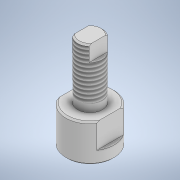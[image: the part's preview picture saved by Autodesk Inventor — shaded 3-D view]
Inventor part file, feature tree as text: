
AUTODESK INVENTOR PART (.ipt)
format: ipt  version: 2021 (Build 250183000, 183)  size: 157,184 bytes
history: native  units: mm
features: sketch x5, extrude x4, chamfer x2, thread x1, hole x1, projected_geometry x1
ambient origin geometry x8: Origin, YZ Plane, XZ Plane, XY Plane, X Axis, Y Axis, Z Axis, Center Point
bodies: Solid1 (feature_tree)
feature tree (14):
  extrude  "Extrusion1"  Depth=12.0mm TaperAngle=0.0deg
  extrude  "Extrusion2"  Depth=8.0mm TaperAngle=0.0deg
  extrude  "Extrusion3"  Depth=19.0mm TaperAngle=0.0deg
  chamfer  "Chamfer1"  Distance=0.5mm Angle=45.0deg
  thread  "Thread1"  [1 undecoded]
  chamfer  "Chamfer2"  Distance=0.5mm Angle=45.0deg
  hole  "Hole1"  [1 undecoded]
  extrude  "Extrusion5"  [1 undecoded]
  sketch  "Sketch1"  dims[d0=15.5mm d1=12.0mm d2=0.0mm]
  sketch  "Sketch2"  dims[d3=12.9mm d4=8.0mm d5=0.0mm]
  projected_geometry  "Projected Loop1"
  sketch  "Sketch3"  dims[d6=8.0mm d7=19.0mm d8=0.0mm d9=0.5mm d10=2.0mm d11=45.0deg d12=16.0mm d13=0.0mm d14=0.5mm d15=2.0mm d16=45.0deg]
  sketch  "Sketch4"  dims[d17=4.917mm d18=10.0mm d19=4.0mm d20=2.0mm d21=90.0deg d22=10.0mm d23=20.594885mm d27=5.4mm]
  sketch  "Sketch6"  dims[d28=5.0mm d29=0.0mm]
note: 3 required parameter values undecoded (feature->parameter linkage not recoverable at this tier; creation-order binding heuristic only, values carry confidence <= 0.55)
